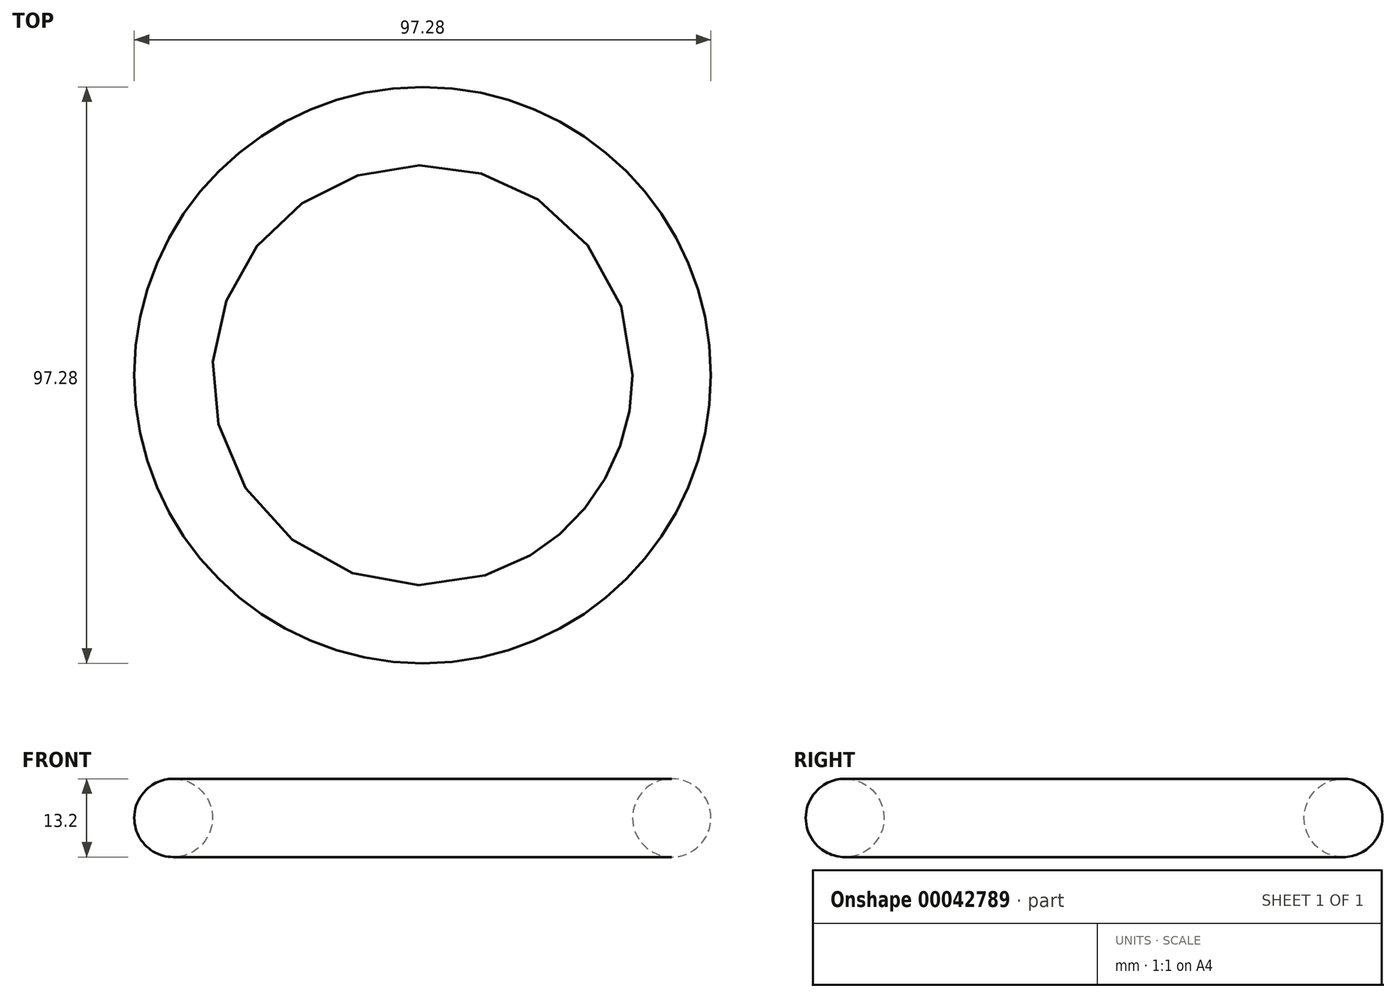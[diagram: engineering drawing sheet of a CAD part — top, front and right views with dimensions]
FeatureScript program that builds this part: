
annotation { "Feature Type Name" : "Feature", "Feature Type Description" : "" }
export const myFeature = defineFeature(function(context is Context, id is Id, definition is map)
    precondition{}
    {
        {
            var Q0;
            Q0=qCreatedBy(makeId("Front.planeOp"),FACE);
            var sketch = newSketch(context, id + "F0", { "sketchPlane" : qUnion([Q0])});
            skLineSegment(sketch, "E0", {"start": v(0, 48.94) * mm, "end": v(0, -49.08) * mm, "construction": true});
            skLineSegment(sketch, "E1", {"start": v(-86.72, 0) * mm, "end": v(93.98, 0) * mm, "construction": true});
            skCircle(sketch, "E2", {"center": v(42.03, 0) * mm, "radius": 6.6 * mm});
            skLineSegment(sketch, "E3", {"start": v(0, 21.88) * mm, "end": v(0, -23.1) * mm});
            skSolve(sketch);
        }
        {
            var Q0;
            Q0 = qSketchRegion(id + "F0", true);
            var Q1;
            Q1=sQuery(id+"F0.wireOp",EDGE,"E3");
            revolve(context, id + "F1", {"entities" : qUnion([Q0]), "axis" : qUnion([Q1]), "revolveType" : RevolveType.FULL});
        }
    });
